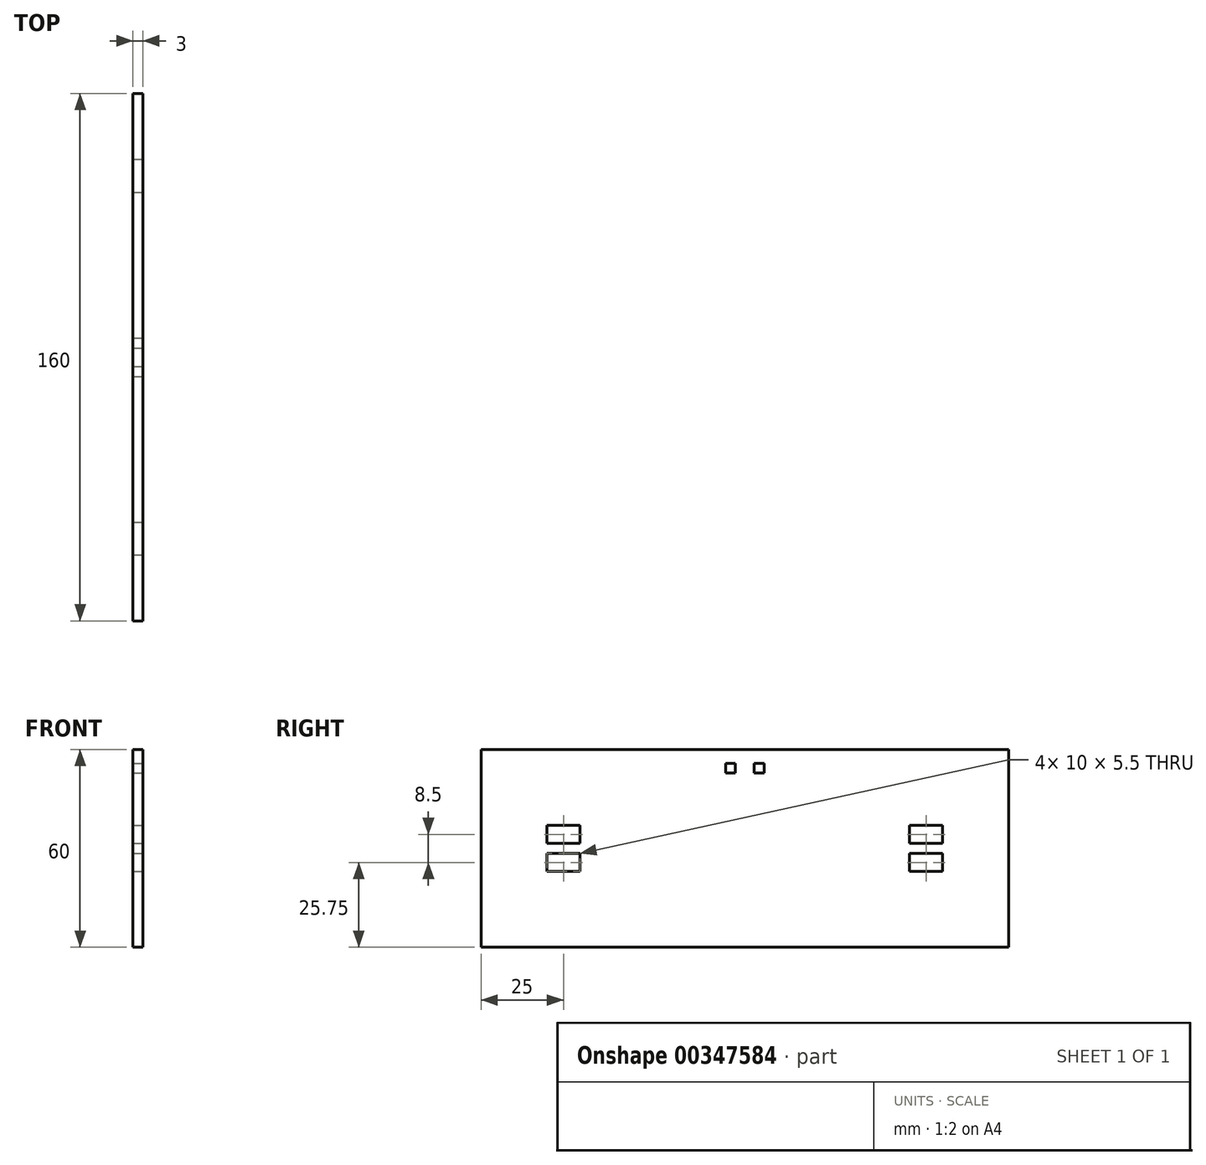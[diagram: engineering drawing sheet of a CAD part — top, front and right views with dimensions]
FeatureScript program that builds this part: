
annotation { "Feature Type Name" : "Feature", "Feature Type Description" : "" }
export const myFeature = defineFeature(function(context is Context, id is Id, definition is map)
    precondition{}
    {
        {
            var Q0;
            Q0=qCreatedBy(makeId("Right.planeOp"),FACE);
            var sketch = newSketch(context, id + "F0", { "sketchPlane" : qUnion([Q0])});
            skLineSegment(sketch, "E0", {"start": v(0, 30) * mm, "end": v(80, 30) * mm});
            skLineSegment(sketch, "E1", {"start": v(80, 30) * mm, "end": v(80, -30) * mm});
            skLineSegment(sketch, "E2", {"start": v(80, -30) * mm, "end": v(0, -30) * mm});
            skLineSegment(sketch, "E3.MirrorCS", {"start": v(0, 30) * mm, "end": v(-80, 30) * mm});
            skLineSegment(sketch, "E4.MirrorCS", {"start": v(-80, 30) * mm, "end": v(-80, -30) * mm});
            skLineSegment(sketch, "E5.MirrorCS", {"start": v(-80, -30) * mm, "end": v(0, -30) * mm});
            skSolve(sketch);
        }
        {
            var Q0;
            Q0=makeQuery(id+"F0.imprint","IMPRINT",FACE,{"disambiguationData":[TD([[makeQuery(id+"F0.imprint","IMPRINT",EDGE,{"derivedFrom":sQuery(id+"F0.wireOp",EDGE,"E0")}),-1.0]])]});
            extrude(context, id + "F1", {"entities" : qUnion([Q0]), "depth" : 3 * mm});
        }
        {
            var Q0;
            Q0=makeQuery(id+"F1.opExtrude","CAP_FACE",FACE,{"disambiguationData":[OSD([sQuery(id+"F0.wireOp",EDGE,"E0"),sQuery(id+"F0.wireOp",EDGE,"E1"),sQuery(id+"F0.wireOp",EDGE,"E2"),sQuery(id+"F0.wireOp",EDGE,"E3.MirrorCS"),sQuery(id+"F0.wireOp",EDGE,"E4.MirrorCS"),sQuery(id+"F0.wireOp",EDGE,"E5.MirrorCS")])],"isStart":false});
            var sketch = newSketch(context, id + "F2", { "sketchPlane" : qUnion([Q0])});
            skLineSegment(sketch, "E6.bottom", {"start": v(-60, 7) * mm, "end": v(-50, 7) * mm});
            skLineSegment(sketch, "E6.top", {"start": v(-60, 1.5) * mm, "end": v(-50, 1.5) * mm});
            skLineSegment(sketch, "E6.left", {"start": v(-60, 7) * mm, "end": v(-60, 1.5) * mm});
            skLineSegment(sketch, "E6.right", {"start": v(-50, 7) * mm, "end": v(-50, 1.5) * mm});
            skLineSegment(sketch, "E7.MirrorCS", {"start": v(-60, -1.5) * mm, "end": v(-50, -1.5) * mm});
            skLineSegment(sketch, "E8.MirrorCS", {"start": v(-60, -7) * mm, "end": v(-60, -1.5) * mm});
            skLineSegment(sketch, "E9.MirrorCS", {"start": v(-60, -7) * mm, "end": v(-50, -7) * mm});
            skLineSegment(sketch, "E10.MirrorCS", {"start": v(-50, -7) * mm, "end": v(-50, -1.5) * mm});
            skLineSegment(sketch, "E11.MirrorCS", {"start": v(60, 7) * mm, "end": v(60, 1.5) * mm});
            skLineSegment(sketch, "E12.MirrorCS", {"start": v(60, 7) * mm, "end": v(50, 7) * mm});
            skLineSegment(sketch, "E13.MirrorCS", {"start": v(50, 7) * mm, "end": v(50, 1.5) * mm});
            skLineSegment(sketch, "E14.MirrorCS", {"start": v(60, 1.5) * mm, "end": v(50, 1.5) * mm});
            skLineSegment(sketch, "E15.MirrorCS", {"start": v(60, -1.5) * mm, "end": v(50, -1.5) * mm});
            skLineSegment(sketch, "E16.MirrorCS", {"start": v(60, -7) * mm, "end": v(60, -1.5) * mm});
            skLineSegment(sketch, "E17.MirrorCS", {"start": v(60, -7) * mm, "end": v(50, -7) * mm});
            skLineSegment(sketch, "E18.MirrorCS", {"start": v(50, -7) * mm, "end": v(50, -1.5) * mm});
            skSolve(sketch);
        }
        {
            var Q0;
            Q0=makeQuery(id+"F2.imprint","IMPRINT",FACE,{"disambiguationData":[TD([[makeQuery(id+"F2.imprint","IMPRINT",EDGE,{"derivedFrom":sQuery(id+"F2.wireOp",EDGE,"E7.MirrorCS")}),-1.0]])]});
            var Q1;
            Q1=makeQuery(id+"F2.imprint","IMPRINT",FACE,{"disambiguationData":[TD([[makeQuery(id+"F2.imprint","IMPRINT",EDGE,{"derivedFrom":sQuery(id+"F2.wireOp",EDGE,"E6.bottom")}),-1.0]])]});
            var Q2;
            Q2=makeQuery(id+"F2.imprint","IMPRINT",FACE,{"disambiguationData":[TD([[makeQuery(id+"F2.imprint","IMPRINT",EDGE,{"derivedFrom":sQuery(id+"F2.wireOp",EDGE,"E11.MirrorCS")}),-1.0]])]});
            var Q3;
            Q3=makeQuery(id+"F2.imprint","IMPRINT",FACE,{"disambiguationData":[TD([[makeQuery(id+"F2.imprint","IMPRINT",EDGE,{"derivedFrom":sQuery(id+"F2.wireOp",EDGE,"E15.MirrorCS")}),1.0]])]});
            extrude(context, id + "F3", {"entities" : qUnion([Q0, Q1, Q2, Q3]), "operationType" : NewBodyOperationType.REMOVE, "oppositeDirection" : true, "depth" : 25 * mm});
        }
        {
            var Q0;
            Q0=makeQuery(id+"F1.opExtrude","CAP_FACE",FACE,{"disambiguationData":[OSD([sQuery(id+"F0.wireOp",EDGE,"E0"),sQuery(id+"F0.wireOp",EDGE,"E1"),sQuery(id+"F0.wireOp",EDGE,"E2"),sQuery(id+"F0.wireOp",EDGE,"E3.MirrorCS"),sQuery(id+"F0.wireOp",EDGE,"E4.MirrorCS"),sQuery(id+"F0.wireOp",EDGE,"E5.MirrorCS")])],"isStart":false});
            var sketch = newSketch(context, id + "F4", { "sketchPlane" : qUnion([Q0])});
            skLineSegment(sketch, "E19.bottom", {"start": v(-5.86, 25.8) * mm, "end": v(-2.84, 25.8) * mm});
            skLineSegment(sketch, "E19.top", {"start": v(-5.86, 22.9) * mm, "end": v(-2.84, 22.9) * mm});
            skLineSegment(sketch, "E19.left", {"start": v(-5.86, 25.8) * mm, "end": v(-5.86, 22.9) * mm});
            skLineSegment(sketch, "E19.right", {"start": v(-2.84, 25.8) * mm, "end": v(-2.84, 22.9) * mm});
            skLineSegment(sketch, "E20.MirrorCS", {"start": v(5.86, 22.9) * mm, "end": v(2.84, 22.9) * mm});
            skLineSegment(sketch, "E21.MirrorCS", {"start": v(2.84, 25.8) * mm, "end": v(2.84, 22.9) * mm});
            skLineSegment(sketch, "E22.MirrorCS", {"start": v(5.86, 25.8) * mm, "end": v(5.86, 22.9) * mm});
            skLineSegment(sketch, "E23.MirrorCS", {"start": v(5.86, 25.8) * mm, "end": v(2.84, 25.8) * mm});
            skSolve(sketch);
        }
        {
            var Q0;
            Q0=makeQuery(id+"F4.imprint","IMPRINT",FACE,{"disambiguationData":[TD([[makeQuery(id+"F4.imprint","IMPRINT",EDGE,{"derivedFrom":sQuery(id+"F4.wireOp",EDGE,"E19.bottom")}),-1.0]])]});
            var Q1;
            Q1=makeQuery(id+"F4.imprint","IMPRINT",FACE,{"disambiguationData":[TD([[makeQuery(id+"F4.imprint","IMPRINT",EDGE,{"derivedFrom":sQuery(id+"F4.wireOp",EDGE,"E20.MirrorCS")}),-1.0]])]});
            extrude(context, id + "F5", {"entities" : qUnion([Q0, Q1]), "operationType" : NewBodyOperationType.REMOVE, "oppositeDirection" : true, "depth" : 25 * mm});
        }
    });
